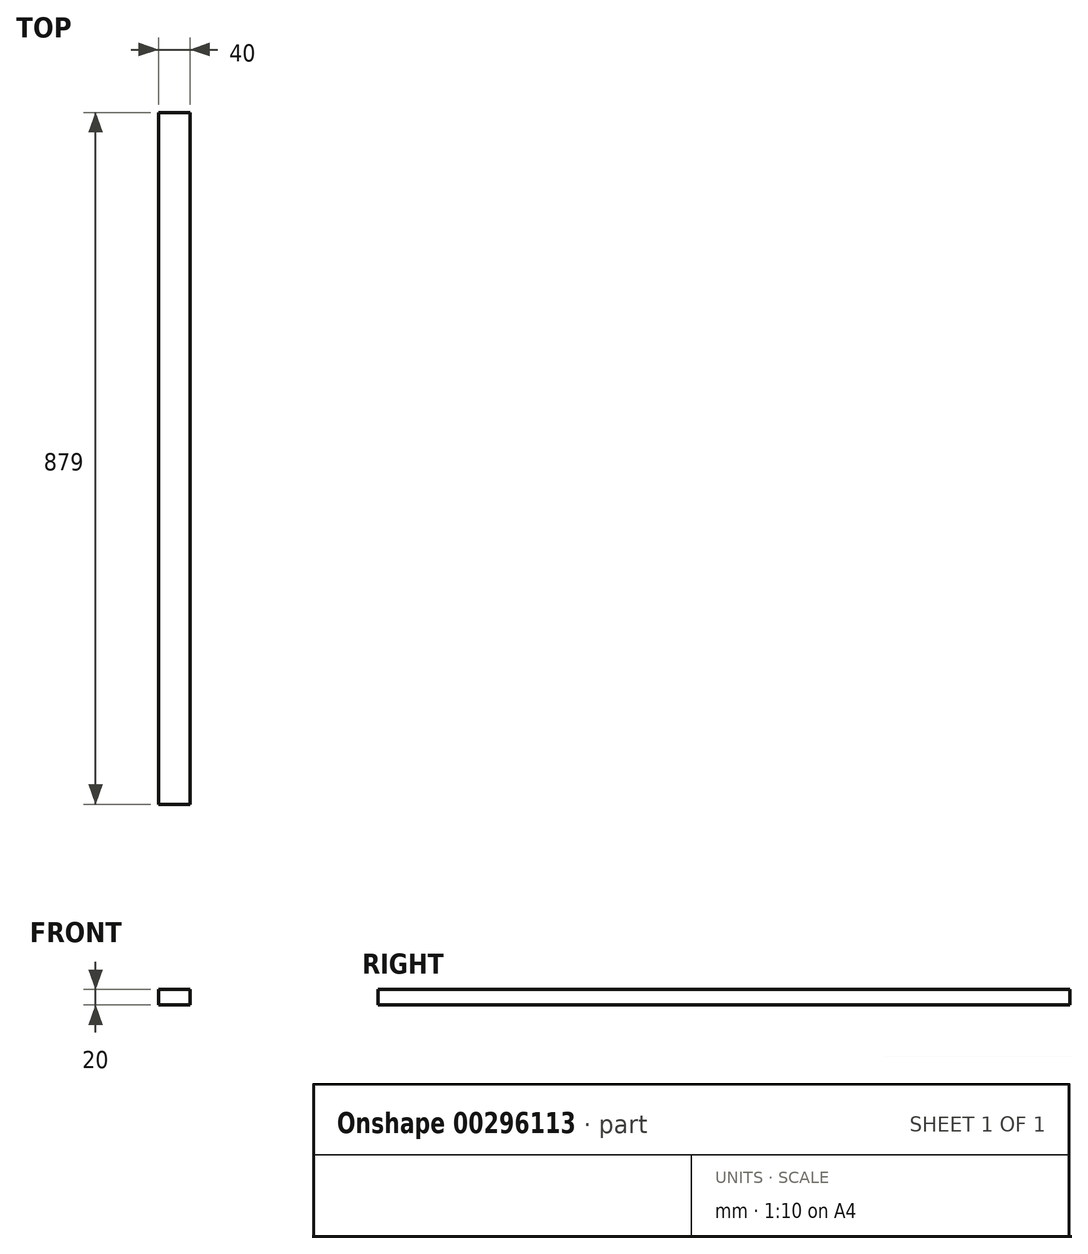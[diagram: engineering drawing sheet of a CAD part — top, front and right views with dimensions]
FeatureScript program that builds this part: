
annotation { "Feature Type Name" : "Feature", "Feature Type Description" : "" }
export const myFeature = defineFeature(function(context is Context, id is Id, definition is map)
    precondition{}
    {
        {
            var Q0;
            Q0=qCreatedBy(makeId("Front.planeOp"),FACE);
            var sketch = newSketch(context, id + "F0", { "sketchPlane" : qUnion([Q0])});
            skLineSegment(sketch, "E0.bottom", {"start": v(20, 10) * mm, "end": v(-20, 10) * mm});
            skLineSegment(sketch, "E0.top", {"start": v(20, -10) * mm, "end": v(-20, -10) * mm});
            skLineSegment(sketch, "E0.left", {"start": v(20, 10) * mm, "end": v(20, -10) * mm});
            skLineSegment(sketch, "E0.right", {"start": v(-20, 10) * mm, "end": v(-20, -10) * mm});
            skPoint(sketch, "E0.middle", {"position": v(0, 0) * mm});
            skSolve(sketch);
        }
        {
            var Q0;
            Q0=makeQuery(id+"F0.imprint","IMPRINT",FACE,{"disambiguationData":[TD([[makeQuery(id+"F0.imprint","IMPRINT",EDGE,{"derivedFrom":sQuery(id+"F0.wireOp",EDGE,"E0.bottom")}),1.0]])]});
            extrude(context, id + "F1", {"entities" : qUnion([Q0]), "oppositeDirection" : true, "depth" : (1000 - 121) * mm});
        }
    });
